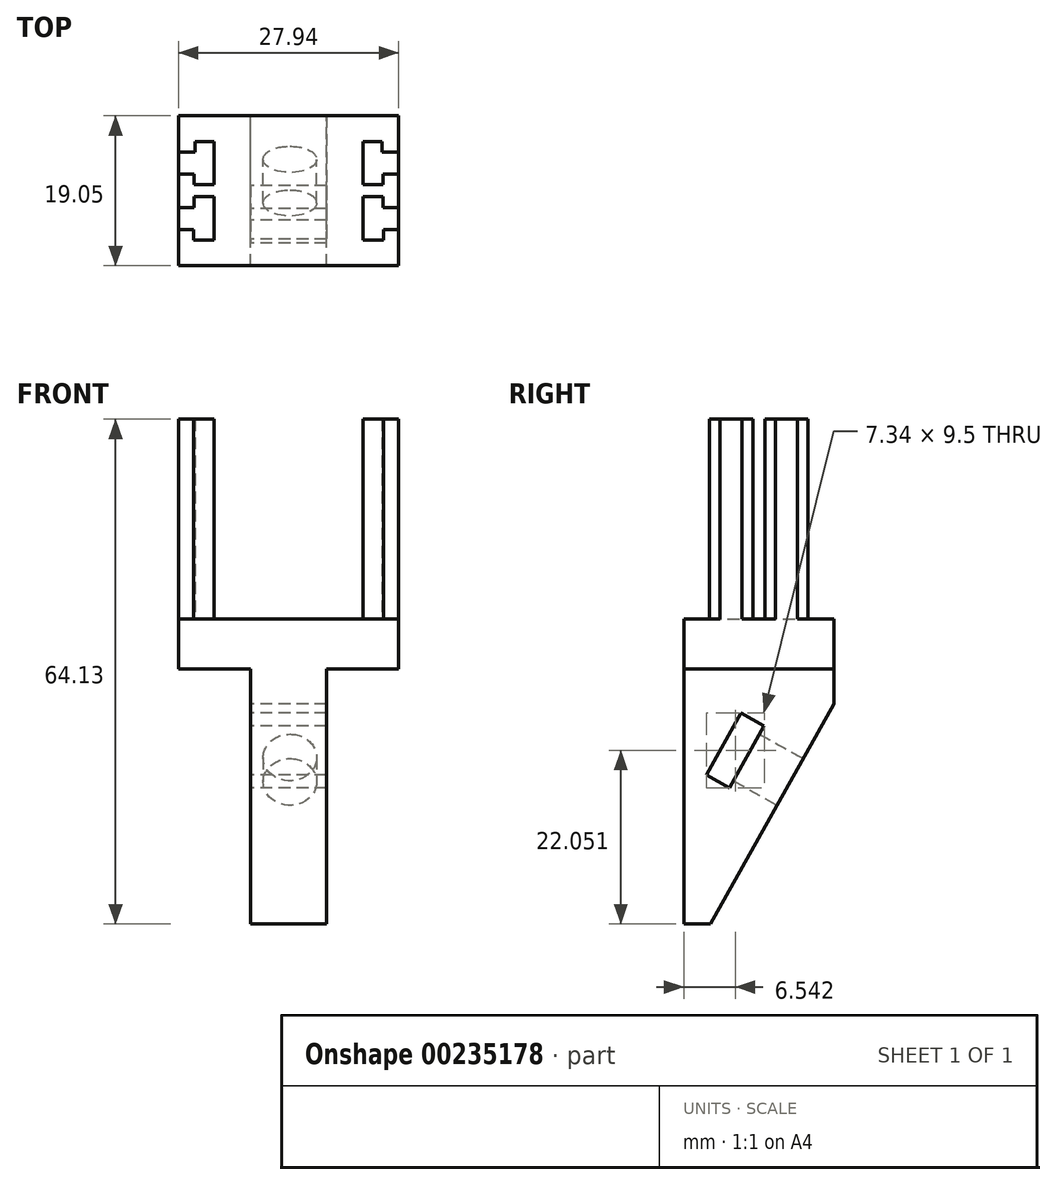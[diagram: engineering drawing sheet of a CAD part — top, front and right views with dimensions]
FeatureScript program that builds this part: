
annotation { "Feature Type Name" : "Feature", "Feature Type Description" : "" }
export const myFeature = defineFeature(function(context is Context, id is Id, definition is map)
    precondition{}
    {
        {
            var Q0;
            Q0=qCreatedBy(makeId("Top.planeOp"),FACE);
            var sketch = newSketch(context, id + "F0", { "sketchPlane" : qUnion([Q0])});
            skLineSegment(sketch, "E0.bottom", {"start": v(0, 0) * mm, "end": v(18.92, 0) * mm});
            skLineSegment(sketch, "E0.top", {"start": v(0, 19.05) * mm, "end": v(18.92, 19.05) * mm});
            skLineSegment(sketch, "E0.left", {"start": v(0, 0) * mm, "end": v(0, 19.05) * mm});
            skLineSegment(sketch, "E0.right", {"start": v(18.92, 0) * mm, "end": v(18.92, 19.05) * mm});
            skLineSegment(sketch, "E1.bottom", {"start": v(-4.5, 19.05) * mm, "end": v(23.43, 19.05) * mm});
            skLineSegment(sketch, "E1.top", {"start": v(-4.5, 0) * mm, "end": v(23.43, 0) * mm});
            skLineSegment(sketch, "E1.left", {"start": v(-4.5, 19.05) * mm, "end": v(-4.5, 0) * mm});
            skLineSegment(sketch, "E1.right", {"start": v(23.43, 19.05) * mm, "end": v(23.43, 0) * mm});
            skSolve(sketch);
        }
        {
            var Q0;
            {var subQ0=sQuery(id+"F0.wireOp",EDGE,"E0.left");Q0=makeQuery(id+"F0.imprint","IMPRINT",FACE,{"disambiguationData":[TD([[makeQuery(id+"F0.imprint","IMPRINT",EDGE,{"derivedFrom":subQ0}),-1.0]])]});}
            var Q1;
            {var subQ0=sQuery(id+"F0.wireOp",EDGE,"E0.left");Q1=makeQuery(id+"F0.imprint","IMPRINT",FACE,{"disambiguationData":[TD([[makeQuery(id+"F0.imprint","IMPRINT",EDGE,{"derivedFrom":subQ0}),1.0]])]});}
            var Q2;
            {var subQ0=sQuery(id+"F0.wireOp",EDGE,"E0.right");Q2=makeQuery(id+"F0.imprint","IMPRINT",FACE,{"disambiguationData":[TD([[makeQuery(id+"F0.imprint","IMPRINT",EDGE,{"derivedFrom":subQ0}),-1.0]])]});}
            extrude(context, id + "F1", {"entities" : qUnion([Q0, Q1, Q2]), "oppositeDirection" : true, "depth" : 6.35 * mm});
        }
        {
            var Q0;
            {var subQ0=sQuery(id+"F0.wireOp",EDGE,"E0.left");Q0=makeQuery(id+"F0.imprint","IMPRINT",FACE,{"disambiguationData":[TD([[makeQuery(id+"F0.imprint","IMPRINT",EDGE,{"derivedFrom":subQ0}),1.0]])]});}
            var sketch = newSketch(context, id + "F2", { "sketchPlane" : qUnion([Q0])});
            skLineSegment(sketch, "E2", {"start": v(0, 10.29) * mm, "end": v(-2.53, 10.29) * mm});
            skLineSegment(sketch, "E3", {"start": v(-2.53, 10.29) * mm, "end": v(-2.53, 11.63) * mm});
            skLineSegment(sketch, "E4", {"start": v(-2.53, 11.63) * mm, "end": v(-4.5, 11.63) * mm});
            skLineSegment(sketch, "E5", {"start": v(-4.5, 11.63) * mm, "end": v(-4.5, 7.42) * mm});
            skLineSegment(sketch, "E6", {"start": v(-4.5, 7.42) * mm, "end": v(-2.53, 7.42) * mm});
            skLineSegment(sketch, "E7", {"start": v(-2.53, 7.42) * mm, "end": v(-2.53, 8.76) * mm});
            skLineSegment(sketch, "E8", {"start": v(-2.53, 8.76) * mm, "end": v(0, 8.76) * mm});
            skLineSegment(sketch, "E9", {"start": v(0, 15.77) * mm, "end": v(-2.43, 15.77) * mm});
            skLineSegment(sketch, "E10", {"start": v(-2.43, 15.77) * mm, "end": v(-2.43, 14.43) * mm});
            skLineSegment(sketch, "E11", {"start": v(-2.43, 14.43) * mm, "end": v(-4.5, 14.43) * mm});
            skLineSegment(sketch, "E12", {"start": v(-4.5, 14.43) * mm, "end": v(-4.5, 19.05) * mm});
            skLineSegment(sketch, "E13", {"start": v(-4.5, 19.05) * mm, "end": v(0, 19.05) * mm});
            skLineSegment(sketch, "E14", {"start": v(0, 15.77) * mm, "end": v(0, 19.05) * mm});
            skLineSegment(sketch, "E15", {"start": v(0, 0) * mm, "end": v(-4.5, 0) * mm});
            skLineSegment(sketch, "E16", {"start": v(-4.5, 0) * mm, "end": v(-4.5, 4.62) * mm});
            skLineSegment(sketch, "E17", {"start": v(-4.5, 4.62) * mm, "end": v(-2.6, 4.62) * mm});
            skLineSegment(sketch, "E18", {"start": v(-2.6, 4.62) * mm, "end": v(-2.6, 3.28) * mm});
            skLineSegment(sketch, "E19", {"start": v(-2.6, 3.28) * mm, "end": v(0, 3.28) * mm});
            skLineSegment(sketch, "E20", {"start": v(0, 3.28) * mm, "end": v(0, 0) * mm});
            skLineSegment(sketch, "E21", {"start": v(0, 8.76) * mm, "end": v(0, 10.29) * mm});
            skLineSegment(sketch, "E22", {"start": v(0, 3.28) * mm, "end": v(0, 8.76) * mm});
            skLineSegment(sketch, "E23", {"start": v(0, 10.29) * mm, "end": v(0, 15.77) * mm});
            skLineSegment(sketch, "E24", {"start": v(9.46, 0) * mm, "end": v(9.46, 19.05) * mm, "construction": true});
            skLineSegment(sketch, "E25.MirrorCS", {"start": v(21.45, 8.76) * mm, "end": v(18.92, 8.76) * mm});
            skLineSegment(sketch, "E26.MirrorCS", {"start": v(18.92, 10.29) * mm, "end": v(21.45, 10.29) * mm});
            skLineSegment(sketch, "E27.MirrorCS", {"start": v(21.45, 10.29) * mm, "end": v(21.45, 11.63) * mm});
            skLineSegment(sketch, "E28.MirrorCS", {"start": v(21.45, 11.63) * mm, "end": v(23.43, 11.63) * mm});
            skLineSegment(sketch, "E29.MirrorCS", {"start": v(23.43, 11.63) * mm, "end": v(23.43, 7.42) * mm});
            skLineSegment(sketch, "E30.MirrorCS", {"start": v(21.45, 7.42) * mm, "end": v(21.45, 8.76) * mm});
            skLineSegment(sketch, "E31.MirrorCS", {"start": v(23.43, 7.42) * mm, "end": v(21.45, 7.42) * mm});
            skLineSegment(sketch, "E32.MirrorCS", {"start": v(21.52, 3.28) * mm, "end": v(18.92, 3.28) * mm});
            skLineSegment(sketch, "E33.MirrorCS", {"start": v(21.52, 4.62) * mm, "end": v(21.52, 3.28) * mm});
            skLineSegment(sketch, "E34.MirrorCS", {"start": v(23.43, 4.62) * mm, "end": v(21.52, 4.62) * mm});
            skLineSegment(sketch, "E35.MirrorCS", {"start": v(23.43, 0) * mm, "end": v(23.43, 4.62) * mm});
            skLineSegment(sketch, "E36.MirrorCS", {"start": v(18.92, 0) * mm, "end": v(23.43, 0) * mm});
            skLineSegment(sketch, "E37.MirrorCS", {"start": v(18.92, 3.28) * mm, "end": v(18.92, 0) * mm});
            skLineSegment(sketch, "E38.MirrorCS", {"start": v(18.92, 3.28) * mm, "end": v(18.92, 8.76) * mm});
            skLineSegment(sketch, "E39.MirrorCS", {"start": v(18.92, 8.76) * mm, "end": v(18.92, 10.29) * mm});
            skLineSegment(sketch, "E40.MirrorCS", {"start": v(18.92, 10.29) * mm, "end": v(18.92, 15.77) * mm});
            skLineSegment(sketch, "E41.MirrorCS", {"start": v(18.92, 15.77) * mm, "end": v(18.92, 19.05) * mm});
            skLineSegment(sketch, "E42.MirrorCS", {"start": v(18.92, 15.77) * mm, "end": v(21.35, 15.77) * mm});
            skLineSegment(sketch, "E43.MirrorCS", {"start": v(21.35, 15.77) * mm, "end": v(21.35, 14.43) * mm});
            skLineSegment(sketch, "E44.MirrorCS", {"start": v(21.35, 14.43) * mm, "end": v(23.43, 14.43) * mm});
            skLineSegment(sketch, "E45.MirrorCS", {"start": v(23.43, 19.05) * mm, "end": v(18.92, 19.05) * mm});
            skLineSegment(sketch, "E46.MirrorCS", {"start": v(23.43, 14.43) * mm, "end": v(23.43, 19.05) * mm});
            skLineSegment(sketch, "E47", {"start": v(-4.5, 11.63) * mm, "end": v(-4.5, 14.43) * mm});
            skLineSegment(sketch, "E48", {"start": v(-4.5, 7.42) * mm, "end": v(-4.5, 4.62) * mm});
            skLineSegment(sketch, "E49", {"start": v(23.43, 4.62) * mm, "end": v(23.43, 7.42) * mm});
            skLineSegment(sketch, "E50", {"start": v(23.43, 11.63) * mm, "end": v(23.43, 14.43) * mm});
            skSolve(sketch);
        }
        {
            var Q0;
            Q0=makeQuery(id+"F2.imprint","IMPRINT",FACE,{"disambiguationData":[TD([[makeQuery(id+"F2.imprint","IMPRINT",EDGE,{"derivedFrom":sQuery(id+"F2.wireOp",EDGE,"E2")}),-1.0]])]});
            var Q1;
            Q1=makeQuery(id+"F2.imprint","IMPRINT",FACE,{"disambiguationData":[TD([[makeQuery(id+"F2.imprint","IMPRINT",EDGE,{"derivedFrom":sQuery(id+"F2.wireOp",EDGE,"E25.MirrorCS")}),1.0]])]});
            var Q2;
            Q2=makeQuery(id+"F2.imprint","IMPRINT",FACE,{"disambiguationData":[TD([[makeQuery(id+"F2.imprint","IMPRINT",EDGE,{"derivedFrom":sQuery(id+"F2.wireOp",EDGE,"E26.MirrorCS")}),1.0]])]});
            var Q3;
            Q3=makeQuery(id+"F2.imprint","IMPRINT",FACE,{"disambiguationData":[TD([[makeQuery(id+"F2.imprint","IMPRINT",EDGE,{"derivedFrom":sQuery(id+"F2.wireOp",EDGE,"E6")}),-1.0]])]});
            extrude(context, id + "F3", {"entities" : qUnion([Q0, Q1, Q2, Q3]), "operationType" : NewBodyOperationType.ADD, "depth" : 25.4 * mm});
        }
        {
            var Q0;
            Q0=makeQuery(id+"F1.opExtrude","CAP_FACE",FACE,{"disambiguationData":[OSD([sQuery(id+"F0.wireOp",EDGE,"E1.bottom"),sQuery(id+"F0.wireOp",EDGE,"E1.top"),sQuery(id+"F0.wireOp",EDGE,"E1.left"),sQuery(id+"F0.wireOp",EDGE,"E1.right")])],"isStart":false});
            var sketch = newSketch(context, id + "F4", { "sketchPlane" : qUnion([Q0])});
            skLineSegment(sketch, "E51.bottom", {"start": v(4.64, 0) * mm, "end": v(14.29, 0) * mm});
            skLineSegment(sketch, "E51.top", {"start": v(4.64, -19.05) * mm, "end": v(14.29, -19.05) * mm});
            skLineSegment(sketch, "E51.left", {"start": v(4.64, 0) * mm, "end": v(4.64, -19.05) * mm});
            skLineSegment(sketch, "E51.right", {"start": v(14.29, 0) * mm, "end": v(14.29, -19.05) * mm});
            skSolve(sketch);
        }
        {
            var Q0;
            Q0=makeQuery(id+"F4.imprint","IMPRINT",FACE,{"disambiguationData":[TD([[makeQuery(id+"F4.imprint","IMPRINT",EDGE,{"derivedFrom":sQuery(id+"F4.wireOp",EDGE,"E51.bottom")}),-1.0]])]});
            extrude(context, id + "F5", {"entities" : qUnion([Q0]), "operationType" : NewBodyOperationType.ADD, "depth" : 32.38 * mm});
        }
        {
            var Q0;
            Q0=makeQuery(id+"F5.opExtrude","SWEPT_FACE",FACE,{"disambiguationData":[OSD([sQuery(id+"F4.wireOp",EDGE,"E51.left")])]});
            var sketch = newSketch(context, id + "F6", { "sketchPlane" : qUnion([Q0])});
            skLineSegment(sketch, "E52", {"start": v(-3.4, -38.74) * mm, "end": v(-19.05, -10.8) * mm});
            skLineSegment(sketch, "E53", {"start": v(-19.05, -10.8) * mm, "end": v(-19.05, -6.35) * mm});
            skLineSegment(sketch, "E54", {"start": v(-19.05, -38.74) * mm, "end": v(4.62, -38.74) * mm, "construction": true});
            skSolve(sketch);
        }
        {
            var Q0;
            {var subQ0=sQuery(id+"F6.wireOp",EDGE,"E52");Q0=makeQuery(id+"F6.imprint","IMPRINT",FACE,{"disambiguationData":[TD([[makeQuery(id+"F6.imprint","IMPRINT",EDGE,{"derivedFrom":subQ0}),1.0]])]});}
            extrude(context, id + "F7", {"entities" : qUnion([Q0]), "operationType" : NewBodyOperationType.REMOVE, "oppositeDirection" : true, "depth" : 25.4 * mm});
        }
        {
            var Q0;
            Q0=makeQuery(id+"F7.boolean.opBoolean","COPY",FACE,{"derivedFrom":makeQuery(id+"F7.opExtrude","SWEPT_FACE",FACE,{"disambiguationData":[OSD([sQuery(id+"F6.wireOp",EDGE,"E52")])]})});
            var sketch = newSketch(context, id + "F8", { "sketchPlane" : qUnion([Q0])});
            skLineSegment(sketch, "E55", {"start": v(-9.46, -0.11) * mm, "end": v(-9.46, -8.04) * mm, "construction": true});
            skCircle(sketch, "E56", {"center": v(-9.64, -11.43) * mm, "radius": 3.4 * mm});
            skLineSegment(sketch, "E57", {"start": v(-9.64, -11.43) * mm, "end": v(-4.64, -11.43) * mm, "construction": true});
            skSolve(sketch);
        }
        {
            var Q0;
            Q0=makeQuery(id+"F8.imprint","IMPRINT",FACE,{"disambiguationData":[TD([[makeQuery(id+"F8.imprint","IMPRINT",EDGE,{"derivedFrom":sQuery(id+"F8.wireOp",EDGE,"E56")}),1.0]])]});
            extrude(context, id + "F9", {"entities" : qUnion([Q0]), "operationType" : NewBodyOperationType.REMOVE, "oppositeDirection" : true, "depth" : 6.35 * mm});
        }
        {
            var Q0;
            {var subQ0=sQuery(id+"F6.wireOp",EDGE,"E52");Q0=makeQuery(id+"F6.imprint","IMPRINT",FACE,{"disambiguationData":[TD([[makeQuery(id+"F6.imprint","IMPRINT",EDGE,{"derivedFrom":subQ0}),-1.0]])]});}
            var sketch = newSketch(context, id + "F10", { "sketchPlane" : qUnion([Q0])});
            skLineSegment(sketch, "E58", {"start": v(-10.21, -13.58) * mm, "end": v(-5.82, -21.43) * mm});
            skLineSegment(sketch, "E59", {"start": v(-5.82, -21.43) * mm, "end": v(-2.87, -19.78) * mm});
            skLineSegment(sketch, "E60", {"start": v(-2.87, -19.78) * mm, "end": v(-7.26, -11.93) * mm});
            skLineSegment(sketch, "E61", {"start": v(-7.26, -11.93) * mm, "end": v(-10.21, -13.58) * mm});
            skLineSegment(sketch, "E62", {"start": v(-13.52, -20.68) * mm, "end": v(-8.02, -17.5) * mm, "construction": true});
            skSolve(sketch);
        }
        {
            var Q0;
            Q0=makeQuery(id+"F10.imprint","IMPRINT",FACE,{"disambiguationData":[TD([[makeQuery(id+"F10.imprint","IMPRINT",EDGE,{"derivedFrom":sQuery(id+"F10.wireOp",EDGE,"E58")}),1.0]])]});
            extrude(context, id + "F11", {"entities" : qUnion([Q0]), "operationType" : NewBodyOperationType.REMOVE, "oppositeDirection" : true, "depth" : 25.4 * mm});
        }
    });
